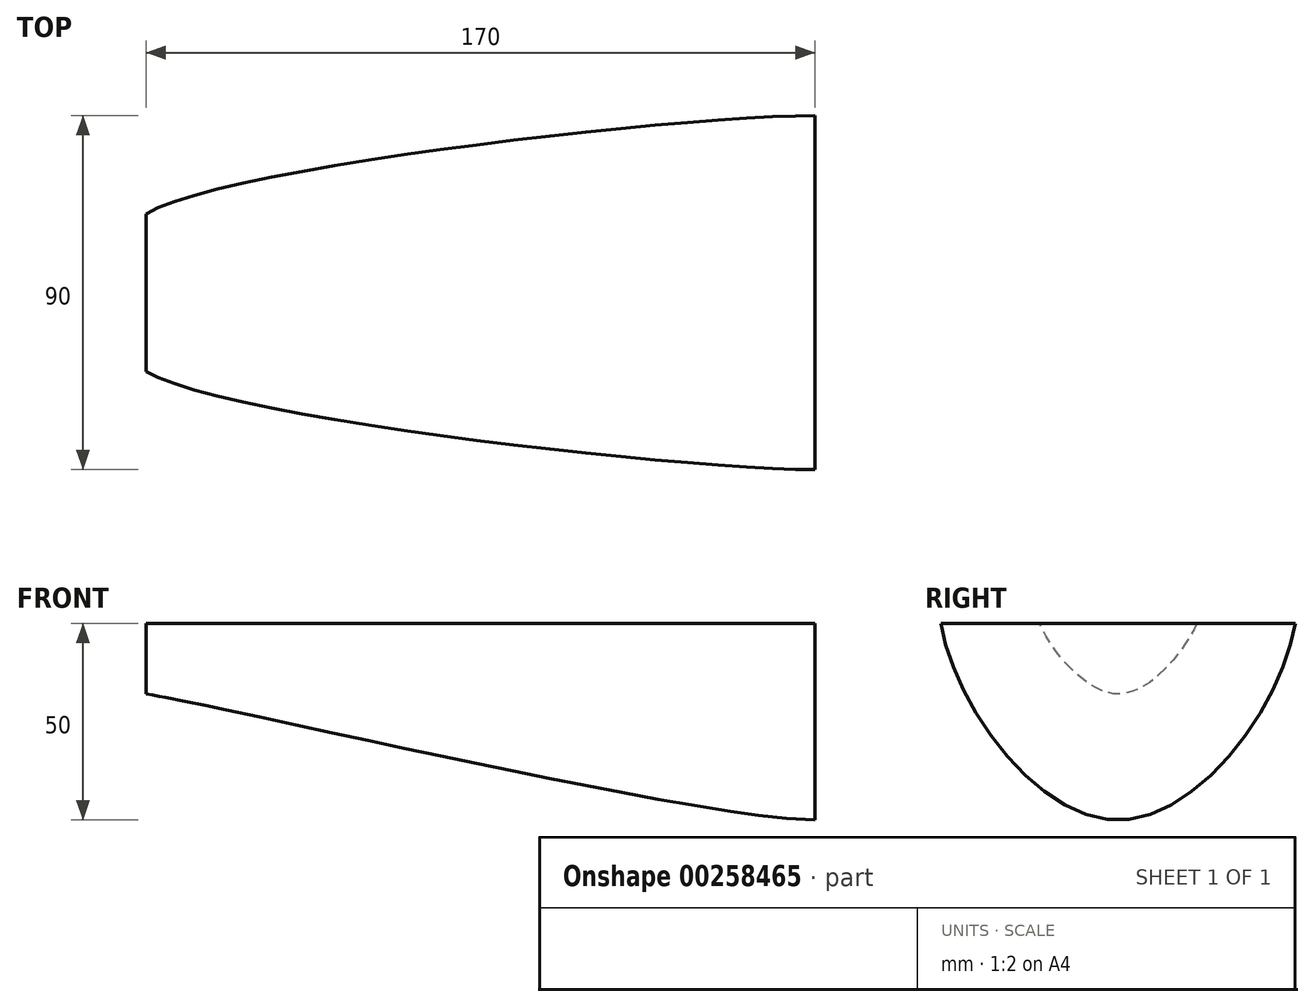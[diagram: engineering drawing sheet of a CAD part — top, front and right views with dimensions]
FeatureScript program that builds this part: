
annotation { "Feature Type Name" : "Feature", "Feature Type Description" : "" }
export const myFeature = defineFeature(function(context is Context, id is Id, definition is map)
    precondition{}
    {
        {
            var Q0;
            Q0=qCreatedBy(makeId("Right.planeOp"),FACE);
            cPlane(context, id + "F0", {"entities" : qUnion([Q0]), "cplaneType" : CPlaneType.OFFSET, "offset" : 170 * mm, "oppositeDirection" : true, "width" : 150 * mm, "height" : 150 * mm});
        }
        {
            var Q0;
            Q0=qCreatedBy(makeId("Right.planeOp"),FACE);
            var sketch = newSketch(context, id + "F1", { "sketchPlane" : qUnion([Q0])});
            skFitSpline(sketch, "E0", {"points": [v(-45, 0) * mm, v(0, -50) * mm, v(45, 0) * mm], "startDerivative": vector(18, -120) * mm, "endDerivative": vector(18, 120) * mm});
            skLineSegment(sketch, "E1", {"start": v(0, 0) * mm, "end": v(-45, 0) * mm});
            skLineSegment(sketch, "E2", {"start": v(0, 0) * mm, "end": v(45, 0) * mm});
            skSolve(sketch);
        }
        {
            var Q0;
            Q0=qCreatedBy(id+"F0.planeOp",FACE);
            var sketch = newSketch(context, id + "F2", { "sketchPlane" : qUnion([Q0])});
            skFitSpline(sketch, "E3", {"points": [v(20, 0) * mm, v(0, -18) * mm, v(-20, 0) * mm], "startDerivative": vector(-12, -30) * mm, "endDerivative": vector(-12, 30) * mm});
            skLineSegment(sketch, "E4", {"start": v(0, 0) * mm, "end": v(20, 0) * mm});
            skLineSegment(sketch, "E5", {"start": v(0, 0) * mm, "end": v(-20, 0) * mm});
            skSolve(sketch);
        }
        {
            var Q0;
            Q0=qCreatedBy(makeId("Front.planeOp"),FACE);
            var sketch = newSketch(context, id + "F3", { "sketchPlane" : qUnion([Q0])});
            skFitSpline(sketch, "E6", {"points": [v(-170, -18) * mm, v(0, -50) * mm], "startDerivative": vector(45, -6) * mm, "endDerivative": vector(87.14, 0) * mm});
            skSolve(sketch);
        }
        {
            var Q0;
            Q0=qCreatedBy(makeId("Top.planeOp"),FACE);
            var sketch = newSketch(context, id + "F4", { "sketchPlane" : qUnion([Q0])});
            skFitSpline(sketch, "E7", {"points": [v(-170, -20) * mm, v(0, -45) * mm], "startDerivative": vector(60, -36) * mm, "endDerivative": vector(105, -0.7) * mm});
            skSolve(sketch);
        }
        {
            var Q0;
            Q0=qCreatedBy(makeId("Top.planeOp"),FACE);
            var sketch = newSketch(context, id + "F5", { "sketchPlane" : qUnion([Q0])});
            skFitSpline(sketch, "E8", {"points": [v(-170, 20) * mm, v(0, 45) * mm], "startDerivative": vector(60, 36) * mm, "endDerivative": vector(105, 0.57) * mm});
            skSolve(sketch);
        }
        {
            var Q0;
            Q0=makeQuery(id+"F1.imprint","IMPRINT",FACE,{"disambiguationData":[TD([[makeQuery(id+"F1.imprint","IMPRINT",EDGE,{"derivedFrom":sQuery(id+"F1.wireOp",EDGE,"E0")}),1.0]])]});
            var Q1;
            Q1=makeQuery(id+"F2.imprint","IMPRINT",FACE,{"disambiguationData":[TD([[makeQuery(id+"F2.imprint","IMPRINT",EDGE,{"derivedFrom":sQuery(id+"F2.wireOp",EDGE,"E3")}),-1.0]])]});
            var Q2;
            Q2=sQuery(id+"F5.wireOp",EDGE,"E8");
            var Q3;
            Q3=sQuery(id+"F4.wireOp",EDGE,"E7");
            var Q4;
            Q4=sQuery(id+"F3.wireOp",EDGE,"E6");
            loft(context, id + "F6", {"addGuides" : true, "sheetProfilesArray" : [{ "sheetProfileEntities" : qUnion([Q0]) }, { "sheetProfileEntities" : qUnion([Q1]) }], "guidesArray" : [{ "guideEntities" : qUnion([Q2]), "guideDerivativeType" : LoftGuideDerivativeType.DEFAULT, "guideDerivativeMagnitude" : 1 }, { "guideEntities" : qUnion([Q3]), "guideDerivativeType" : LoftGuideDerivativeType.DEFAULT, "guideDerivativeMagnitude" : 1 }, { "guideEntities" : qUnion([Q4]), "guideDerivativeType" : LoftGuideDerivativeType.DEFAULT, "guideDerivativeMagnitude" : 1 }]});
        }
    });
